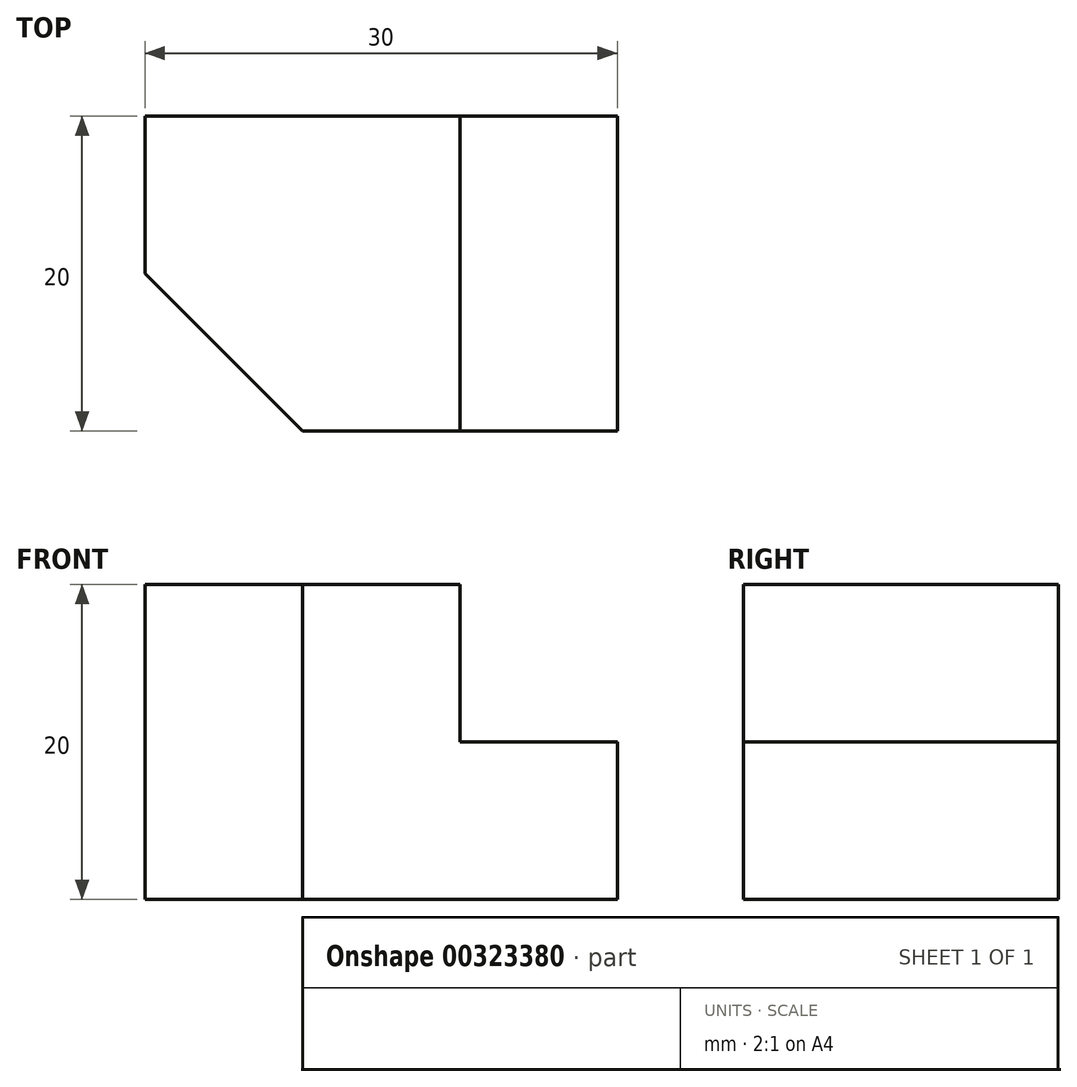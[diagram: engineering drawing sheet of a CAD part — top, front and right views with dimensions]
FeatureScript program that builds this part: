
annotation { "Feature Type Name" : "Feature", "Feature Type Description" : "" }
export const myFeature = defineFeature(function(context is Context, id is Id, definition is map)
    precondition{}
    {
        {
            var Q0;
            Q0=qCreatedBy(makeId("Front.planeOp"),FACE);
            var sketch = newSketch(context, id + "F0", { "sketchPlane" : qUnion([Q0])});
            skLineSegment(sketch, "E0", {"start": v(-20, 10) * mm, "end": v(-20, -10) * mm});
            skLineSegment(sketch, "E1", {"start": v(-20, -10) * mm, "end": v(10, -10) * mm});
            skLineSegment(sketch, "E2", {"start": v(10, -10) * mm, "end": v(10, 0) * mm});
            skLineSegment(sketch, "E3", {"start": v(10, 0) * mm, "end": v(0, 0) * mm});
            skLineSegment(sketch, "E4", {"start": v(0, 0) * mm, "end": v(0, 10) * mm});
            skLineSegment(sketch, "E5", {"start": v(0, 10) * mm, "end": v(-20, 10) * mm});
            skSolve(sketch);
        }
        {
            var Q0;
            Q0 = qSketchRegion(id + "F0", true);
            extrude(context, id + "F1", {"entities" : qUnion([Q0]), "depth" : 20 * mm});
        }
        {
            var Q0;
            Q0=makeQuery(id+"F1.opExtrude","SWEPT_FACE",FACE,{"disambiguationData":[OSD([sQuery(id+"F0.wireOp",EDGE,"E5")])]});
            var sketch = newSketch(context, id + "F2", { "sketchPlane" : qUnion([Q0])});
            skLineSegment(sketch, "E6", {"start": v(-20, -10) * mm, "end": v(-10, -20) * mm});
            skLineSegment(sketch, "E7", {"start": v(-10, -20) * mm, "end": v(-20, -20) * mm});
            skLineSegment(sketch, "E8", {"start": v(-20, -20) * mm, "end": v(-20, -10) * mm});
            skSolve(sketch);
        }
        {
            var Q0;
            Q0=makeQuery(id+"F2.imprint","IMPRINT",FACE,{"disambiguationData":[TD([[makeQuery(id+"F2.imprint","IMPRINT",EDGE,{"derivedFrom":sQuery(id+"F2.wireOp",EDGE,"E6")}),-1.0]])]});
            extrude(context, id + "F3", {"entities" : qUnion([Q0]), "operationType" : NewBodyOperationType.REMOVE, "oppositeDirection" : true, "depth" : 25 * mm});
        }
    });
